# Revit family: CADS_Vent-Axia_Lo-CarbonSentinel_Econiq_L_MVHR
name_source: partatom
category: Mechanical Equipment
units: mm (PartAtom-declared; Revit-internal decimal feet)

## family parameters
Always vertical = Yes
Cut with Voids When Loaded = No
OmniClass Number = 23.75.00.00
OmniClass Title = Climate Control (HVAC)
Part Type = Normal
Room Calculation Point = No
Round Connector Dimension = Use Diameter
Shared = No
Work Plane-Based = No

## types (2) — shared parameters
AirflowRateRange = 200.0 L/s
Apparent Load = 0 VA
AssemblyPlace = FACTORY
AssetType = Fixed
Category = Pr_60_60_36:Heat recovery distribution equipment
Color = White
Description = Sentinel Econiq L
DevelopedFor = Vent-Axia
DurationUnit = year
ExpectedLife = 20
ExpectedServiceLife = 15
Features = Humidistat
Fitting Type = Ignore
GrossWeight = 50.00 kg
HasProtectiveEarth = Yes
IP_Code = IPX2
IfcExportAs = IfcAirToAirHeatRecoveryType
IfcExportType = USERDEFINED
IsExtendedWarranty = No
Manufacturer = Vent-Axia Limited
Material = ABS Plastic
Model = 499641
ModelNumber = 499641
ModelReference = Sentinel Econiq L
Name = MVHR Unit
NominalHeight = 931 mm  [stored 3.05446 ft]
NominalLength = 728 mm  [stored 2.38845 ft]
NominalWidth = 608 mm  [stored 1.99475 ft]
NumberOfPoles = 1
ProductionYear = 2020
Quantity = 1
RatedCurrent = 0 A
RatedVoltage = 240 V
ServiceLifeDuration = 20
Shape = Rectangular
Size = 608mm x728mm x931mm
SpigotConnLength = 237 mm  [stored 0.777559 ft]
SpigotConnWidth = 237 mm  [stored 0.777559 ft]
SpigotCrsLength = 520 mm  [stored 1.70604 ft]
SpigotCrsWidth = 261 mm
SpigotHeight = 50 mm  [stored 0.164042 ft]
SpigotOffset = 135 mm  [stored 0.442913 ft]
Status = New
TemperatureRange = -20°C to+40°C
Type Image = <None>
Version = 1.0
WarrantyDurationLabor = 2
WarrantyDurationMotors = 5
WarrantyDurationParts = 2
WarrantyDurationUnit = year
WorkingPressure = 0.0 Pa
zero-valued in all types: CADS_Index, Default Elevation

## per-type parameters (varying)
| type | LeftHand | RightHand |
| Sentinel Econiq L Right Hand | No | Yes |
| Sentinel Econiq L Left Hand | Yes | No |

note: [stored X ft] marks values corroborated as IEEE doubles in the binary element streams (Revit-internal decimal feet)

## geometry (parser evidence)
native form markers: Sweep x14
no freeform markers — native parametric forms only
